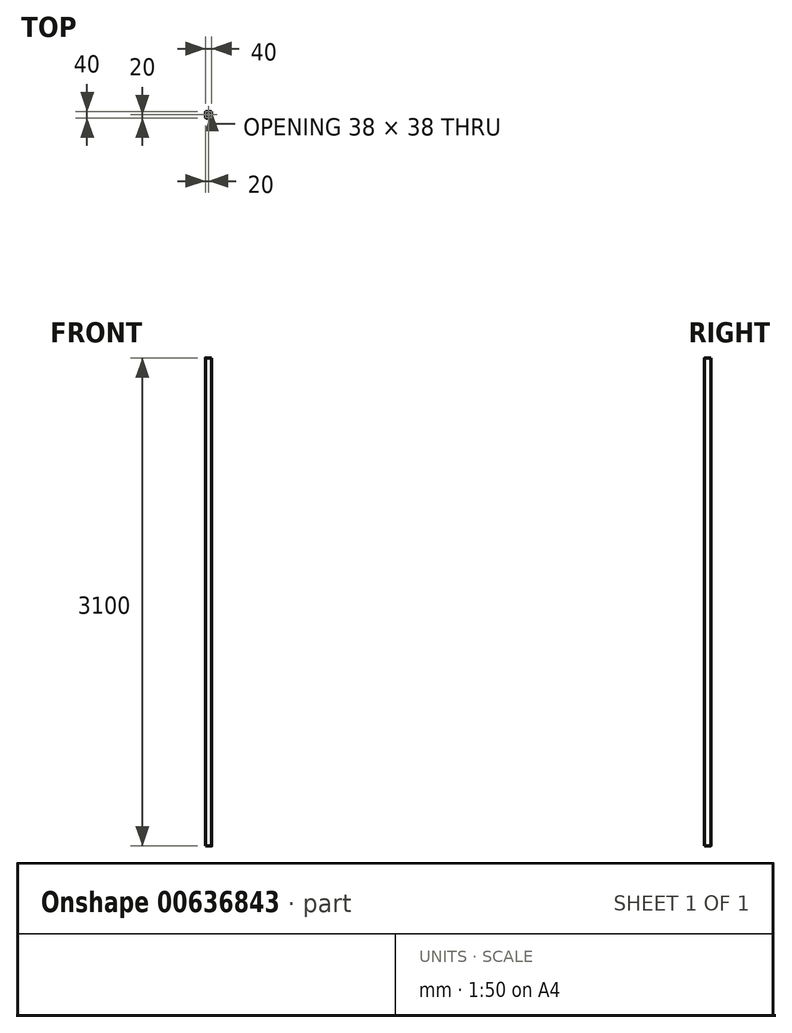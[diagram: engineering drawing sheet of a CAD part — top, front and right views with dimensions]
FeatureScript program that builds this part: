
annotation { "Feature Type Name" : "Feature", "Feature Type Description" : "" }
export const myFeature = defineFeature(function(context is Context, id is Id, definition is map)
    precondition{}
    {
        {
            var Q0;
            Q0=qCreatedBy(makeId("Top.planeOp"),FACE);
            var sketch = newSketch(context, id + "F0", { "sketchPlane" : qUnion([Q0])});
            skLineSegment(sketch, "E0.bottom", {"start": v(16, -20) * mm, "end": v(-16, -20) * mm});
            skLineSegment(sketch, "E0.top", {"start": v(16, 20) * mm, "end": v(-16, 20) * mm});
            skLineSegment(sketch, "E0.left", {"start": v(20, -16) * mm, "end": v(20, 16) * mm});
            skLineSegment(sketch, "E0.right", {"start": v(-20, -16) * mm, "end": v(-20, 16) * mm});
            skPoint(sketch, "E0.middle", {"position": v(0, 0) * mm});
            skPoint(sketch, "E1.visualSharp", {"position": v(-20, 20) * mm});
            skArc(sketch, "E1.filletArc", {"start": v(-16, 20) * mm, "mid": v(-18.83, 18.83) * mm, "end": v(-20, 16) * mm});
            skPoint(sketch, "E2.visualSharp", {"position": v(20, 20) * mm});
            skArc(sketch, "E2.filletArc", {"start": v(20, 16) * mm, "mid": v(18.83, 18.83) * mm, "end": v(16, 20) * mm});
            skPoint(sketch, "E3.visualSharp", {"position": v(20, -20) * mm});
            skArc(sketch, "E3.filletArc", {"start": v(16, -20) * mm, "mid": v(18.83, -18.83) * mm, "end": v(20, -16) * mm});
            skPoint(sketch, "E4.visualSharp", {"position": v(-20, -20) * mm});
            skArc(sketch, "E4.filletArc", {"start": v(-20, -16) * mm, "mid": v(-18.83, -18.83) * mm, "end": v(-16, -20) * mm});
            skLineSegment(sketch, "E5.0", {"start": v(16, 19) * mm, "end": v(-16, 19) * mm});
            skLineSegment(sketch, "E6.0", {"start": v(16, -19) * mm, "end": v(-16, -19) * mm});
            skLineSegment(sketch, "E7.0", {"start": v(19, -16) * mm, "end": v(19, 16) * mm});
            skLineSegment(sketch, "E8.0", {"start": v(-19, -16) * mm, "end": v(-19, 16) * mm});
            skArc(sketch, "E9.filletArc", {"start": v(19, 16) * mm, "mid": v(18.12, 18.12) * mm, "end": v(16, 19) * mm});
            skArc(sketch, "E10.filletArc", {"start": v(-16, 19) * mm, "mid": v(-18.12, 18.12) * mm, "end": v(-19, 16) * mm});
            skArc(sketch, "E11.filletArc", {"start": v(-19, -16) * mm, "mid": v(-18.12, -18.12) * mm, "end": v(-16, -19) * mm});
            skArc(sketch, "E12.filletArc", {"start": v(16, -19) * mm, "mid": v(18.12, -18.12) * mm, "end": v(19, -16) * mm});
            skSolve(sketch);
        }
        {
            var Q0;
            Q0 = qSketchRegion(id + "F0", true);
            extrude(context, id + "F1", {"entities" : qUnion([Q0]), "flatOperationType" : FlatOperationType.REMOVE, "depth" : 3100 * mm, "offsetDistance" : 25 * mm, "domain" : OperationDomain.MODEL});
        }
    });
